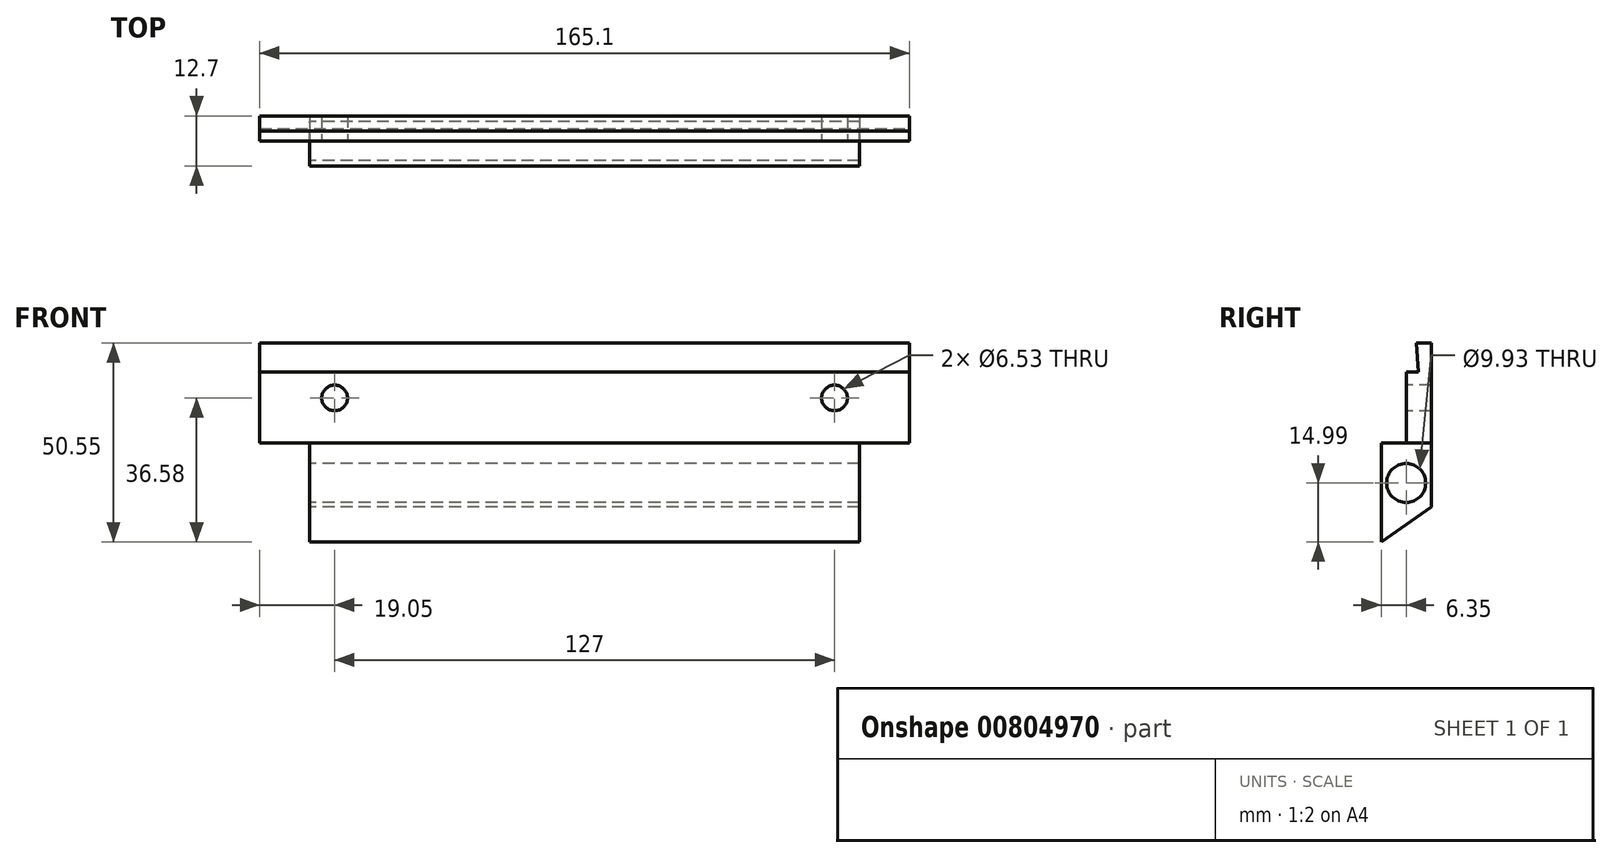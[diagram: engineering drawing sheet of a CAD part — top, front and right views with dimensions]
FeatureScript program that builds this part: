
annotation { "Feature Type Name" : "Feature", "Feature Type Description" : "" }
export const myFeature = defineFeature(function(context is Context, id is Id, definition is map)
    precondition{}
    {
        {
            var Q0;
            Q0=qCreatedBy(makeId("Front.planeOp"),FACE);
            var sketch = newSketch(context, id + "F0", { "sketchPlane" : qUnion([Q0])});
            skLineSegment(sketch, "E0.bottom", {"start": v(0, 0) * mm, "end": v(165.1, 0) * mm});
            skLineSegment(sketch, "E0.top", {"start": v(0, 38.1) * mm, "end": v(165.1, 38.1) * mm});
            skLineSegment(sketch, "E0.left", {"start": v(0, 0) * mm, "end": v(0, 38.1) * mm});
            skLineSegment(sketch, "E0.right", {"start": v(165.1, 0) * mm, "end": v(165.1, 38.1) * mm});
            skSolve(sketch);
        }
        {
            var Q0;
            Q0=qSketchRegion(id+"F0",true);
            extrude(context, id + "F1", {"entities" : qUnion([Q0]), "depth" : 12.7 * mm, "offsetDistance" : 25.4 * mm});
        }
        {
            var Q0;
            Q0=makeQuery(id+"F1.opExtrude","SWEPT_FACE",FACE,{"disambiguationData":[OSD([sQuery(id+"F0.wireOp",EDGE,"E0.right")])]});
            var sketch = newSketch(context, id + "F2", { "sketchPlane" : qUnion([Q0])});
            skLineSegment(sketch, "E1", {"start": v(-6.35, 30.73) * mm, "end": v(-3.21, 30.73) * mm});
            skLineSegment(sketch, "E2", {"start": v(-3.21, 30.73) * mm, "end": v(-3.81, 38.1) * mm});
            skLineSegment(sketch, "E3", {"start": v(-3.81, 38.1) * mm, "end": v(-8.9, 38.1) * mm});
            skLineSegment(sketch, "E4", {"start": v(-12.7, 27.76) * mm, "end": v(-12.7, 38.1) * mm});
            skLineSegment(sketch, "E5", {"start": v(-12.7, 38.1) * mm, "end": v(-8.9, 38.1) * mm});
            skLineSegment(sketch, "E6", {"start": v(-6.35, 30.73) * mm, "end": v(-6.35, 12.7) * mm});
            skLineSegment(sketch, "E7", {"start": v(-6.35, 12.7) * mm, "end": v(-12.7, 12.7) * mm});
            skLineSegment(sketch, "E8", {"start": v(-12.7, 12.7) * mm, "end": v(-12.7, 27.76) * mm});
            skSolve(sketch);
        }
        {
            var Q0;
            Q0=qSketchRegion(id+"F2",true);
            extrude(context, id + "F3", {"entities" : qUnion([Q0]), "operationType" : NewBodyOperationType.REMOVE, "endBound" : BoundingType.THROUGH_ALL, "oppositeDirection" : true, "depth" : 25.4 * mm, "offsetDistance" : 25.4 * mm});
        }
        {
            var Q0;
            Q0=makeQuery(id+"F1.opExtrude","CAP_FACE",FACE,{"disambiguationData":[OSD([sQuery(id+"F0.wireOp",EDGE,"E0.bottom"),sQuery(id+"F0.wireOp",EDGE,"E0.top"),sQuery(id+"F0.wireOp",EDGE,"E0.left"),sQuery(id+"F0.wireOp",EDGE,"E0.right")])],"isStart":false});
            var sketch = newSketch(context, id + "F4", { "sketchPlane" : qUnion([Q0])});
            skLineSegment(sketch, "E9.bottom", {"start": v(0, 0) * mm, "end": v(165.1, 0) * mm});
            skLineSegment(sketch, "E9.top", {"start": v(0, -12.7) * mm, "end": v(165.1, -12.7) * mm});
            skLineSegment(sketch, "E9.left", {"start": v(0, 0) * mm, "end": v(0, -12.7) * mm});
            skLineSegment(sketch, "E9.right", {"start": v(165.1, 0) * mm, "end": v(165.1, -12.7) * mm});
            skSolve(sketch);
        }
        {
            var Q0;
            Q0 = qSketchRegion(id + "F4", true);
            extrude(context, id + "F5", {"entities" : qUnion([Q0]), "operationType" : NewBodyOperationType.ADD, "oppositeDirection" : true, "depth" : 12.7 * mm, "offsetDistance" : 25.4 * mm});
        }
        {
            var Q0;
            Q0=makeQuery(id+"F3.boolean.opBoolean","COPY",FACE,{"derivedFrom":makeQuery(id+"F3.opExtrude","SWEPT_FACE",FACE,{"disambiguationData":[OSD([sQuery(id+"F2.wireOp",EDGE,"E6")])]})});
            var sketch = newSketch(context, id + "F6", { "sketchPlane" : qUnion([Q0])});
            skPoint(sketch, "E10", {"position": v(19.05, 24.13) * mm});
            skPoint(sketch, "E10.positionSnap0", {"position": v(-12.7, 24.13) * mm});
            skPoint(sketch, "E11", {"position": v(82.55, 24.13) * mm});
            skPoint(sketch, "E12", {"position": v(146.05, 24.13) * mm});
            skPoint(sketch, "E13", {"position": v(82.55, 30.73) * mm});
            skSolve(sketch);
        }
        {
            var Q0;
            Q0=sQuery(id+"F6.wireOp",VERTEX,"E10");
            var Q1;
            Q1=sQuery(id+"F6.wireOp",VERTEX,"E12");
            var Q2;
            Q2=makeQuery(id+"F1.opExtrude","SWEPT_BODY",BODY,{"disambiguationData":[OSD([sQuery(id+"F0.wireOp",EDGE,"E0.bottom"),sQuery(id+"F0.wireOp",EDGE,"E0.top"),sQuery(id+"F0.wireOp",EDGE,"E0.left"),sQuery(id+"F0.wireOp",EDGE,"E0.right")])]});
            hole(context, id + "F7", {"style" : HoleStyle.SIMPLE, "endStyle" : HoleEndStyle.THROUGH, "standardTappedOrClearance" : lookupTablePath({ "standard" : "ANSI", "engagement" : "75%", "pitch" : "18 tpi", "size" : "5/16", "type" : "Tapped" }), "standardBlindInLast" : lookupTablePath({ "standard" : "ANSI", "engagement" : "75%", "pitch" : "18 tpi", "size" : "5/16", "type" : "Tapped" }), "holeDiameter" : 6.53 * mm, "majorDiameter" : 7.94 * mm, "showTappedDepth" : true, "isTappedThrough" : true, "tappedDepth" : 0.85 * mm, "tapClearance" : 3, "startFromSketch" : true, "locations" : qUnion([Q0, Q1]), "scope" : qUnion([Q2])});
        }
        {
            var Q0;
            Q0=makeQuery(id+"Fep4zfGRUDcCQot_1.boolean.opBoolean","MERGE",FACE,{"derivedFrom":[makeQuery(id+"F1.opExtrude","SWEPT_FACE",FACE,{"disambiguationData":[OSD([sQuery(id+"F0.wireOp",EDGE,"E0.left")])]}),makeQuery(id+"Fep4zfGRUDcCQot_1.opExtrude","CAP_FACE",FACE,{"disambiguationData":[OSD([dummyQuery(id+"Fep4zfGRUDcCQot_1.vertexPlane.planeOp",FACE)])],"isStart":false})]});
            var sketch = newSketch(context, id + "F8", { "sketchPlane" : qUnion([Q0])});
            skPoint(sketch, "E14", {"position": v(6.35, 2.54) * mm});
            skSolve(sketch);
        }
        {
            var Q0;
            Q0=makeQuery(id+"Fep4zfGRUDcCQot_1.boolean.opBoolean","MERGE",FACE,{"derivedFrom":[makeQuery(id+"F1.opExtrude","CAP_FACE",FACE,{"disambiguationData":[OSD([sQuery(id+"F0.wireOp",EDGE,"E0.bottom"),sQuery(id+"F0.wireOp",EDGE,"E0.top"),sQuery(id+"F0.wireOp",EDGE,"E0.left"),sQuery(id+"F0.wireOp",EDGE,"E0.right")])],"isStart":false}),makeQuery(id+"Fep4zfGRUDcCQot_1.opExtrude","SWEPT_FACE",FACE,{"disambiguationData":[OSD([sQuery(id+"Ff5Muxxik2Xf4fX_1.wireOp",EDGE,"I0QTpEE2-04dR-5V9a-7yra-vEzluYwGXqzQ")])]})]});
            var sketch = newSketch(context, id + "F9", { "sketchPlane" : qUnion([Q0])});
            skLineSegment(sketch, "E15.bottom", {"start": v(0, -12.7) * mm, "end": v(12.7, -12.7) * mm});
            skLineSegment(sketch, "E15.top", {"start": v(0, 12.7) * mm, "end": v(12.7, 12.7) * mm});
            skLineSegment(sketch, "E15.left", {"start": v(0, -12.7) * mm, "end": v(0, 12.7) * mm});
            skLineSegment(sketch, "E15.right", {"start": v(12.7, -12.7) * mm, "end": v(12.7, 12.7) * mm});
            skLineSegment(sketch, "E16.bottom", {"start": v(82.55, -12.7) * mm, "end": v(69.85, -12.7) * mm, "construction": true});
            skLineSegment(sketch, "E16.top", {"start": v(82.55, 12.7) * mm, "end": v(69.85, 12.7) * mm, "construction": true});
            skLineSegment(sketch, "E16.right", {"start": v(69.85, -12.7) * mm, "end": v(69.85, 12.7) * mm, "construction": true});
            skLineSegment(sketch, "E17.bottom", {"start": v(165.1, -12.7) * mm, "end": v(152.4, -12.7) * mm});
            skLineSegment(sketch, "E17.top", {"start": v(165.1, 12.7) * mm, "end": v(152.4, 12.7) * mm});
            skLineSegment(sketch, "E17.left", {"start": v(165.1, -12.7) * mm, "end": v(165.1, 12.7) * mm});
            skLineSegment(sketch, "E17.right", {"start": v(152.4, -12.7) * mm, "end": v(152.4, 12.7) * mm});
            skLineSegment(sketch, "E18", {"start": v(82.55, 12.7) * mm, "end": v(82.55, 0) * mm, "construction": true});
            skLineSegment(sketch, "E19.MirrorCS", {"start": v(95.25, -12.7) * mm, "end": v(95.25, 12.7) * mm, "construction": true});
            skLineSegment(sketch, "E20.MirrorCS", {"start": v(82.55, 12.7) * mm, "end": v(95.25, 12.7) * mm, "construction": true});
            skLineSegment(sketch, "E21.MirrorCS", {"start": v(82.55, -12.7) * mm, "end": v(95.25, -12.7) * mm, "construction": true});
            skSolve(sketch);
        }
        {
            var Q0;
            Q0 = qSketchRegion(id + "F9", true);
            extrude(context, id + "F10", {"entities" : qUnion([Q0]), "operationType" : NewBodyOperationType.REMOVE, "endBound" : BoundingType.THROUGH_ALL, "oppositeDirection" : true, "depth" : 25.4 * mm, "offsetDistance" : 25.4 * mm});
        }
        {
            var Q0;
            Q0=sQuery(id+"F8.wireOp",VERTEX,"E14");
            var Q1;
            Q1=makeQuery(id+"F1.opExtrude","SWEPT_BODY",BODY,{"disambiguationData":[OSD([sQuery(id+"F0.wireOp",EDGE,"E0.bottom"),sQuery(id+"F0.wireOp",EDGE,"E0.top"),sQuery(id+"F0.wireOp",EDGE,"E0.left"),sQuery(id+"F0.wireOp",EDGE,"E0.right")])]});
            hole(context, id + "F11", {"style" : HoleStyle.SIMPLE, "endStyle" : HoleEndStyle.THROUGH, "standardTappedOrClearance" : lookupTablePath({ "fit" : "Close (ASME)", "standard" : "ANSI", "size" : "3/8", "type" : "Clearance" }), "standardBlindInLast" : lookupTablePath({ "fit" : "Close (ASME)", "standard" : "ANSI", "engagement" : "75%", "pitch" : "16 tpi", "size" : "3/8", "type" : "Clearance & tapped" }), "holeDiameter" : 9.93 * mm, "majorDiameter" : 9.52 * mm, "isTappedThrough" : true, "tappedDepth" : 2.12 * mm, "tapClearance" : 3, "startFromSketch" : true, "locations" : qUnion([Q0]), "scope" : qUnion([Q1])});
        }
        {
            var Q0;
            Q0=makeQuery(id+"F5.opExtrude","CAP_EDGE",EDGE,{"disambiguationData":[OSD([sQuery(id+"F4.wireOp",EDGE,"E9.top")])],"isStart":false});
            chamfer(context, id + "F12", {"entities" : qUnion([Q0]), "chamferType" : ChamferType.OFFSET_ANGLE, "width" : 9.14 * mm, "oppositeDirection" : true, "angle" : 55 * degree});
        }
    });
